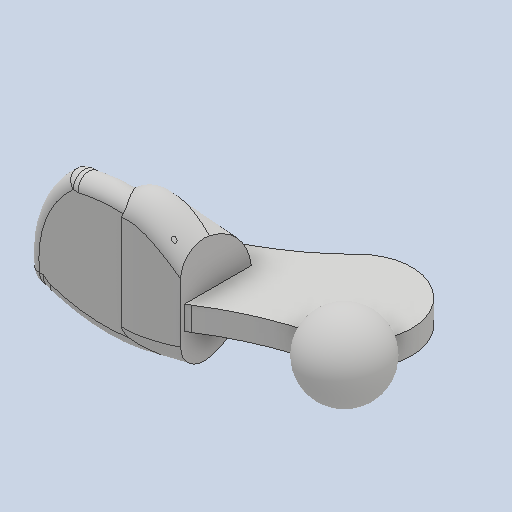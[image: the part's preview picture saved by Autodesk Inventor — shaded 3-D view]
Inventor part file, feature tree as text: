
AUTODESK INVENTOR PART (.ipt)
format: ipt  version: 2024.2 (Build 282272000, 272)  size: 452,096 bytes
history: native  units: mm
features: other x10, sketch x5, extrude x3, fillet x2, revolve x1, loft x1
ambient origin geometry x8: Origin, YZ Plane, XZ Plane, XY Plane, X Axis, Y Axis, Z Axis, Center Point
bodies: Body1 (feature_tree), Body2 (feature_tree), Body3 (feature_tree)
feature tree (22):
  other  "Твердое тело1"
  sketch  "Эскиз1"
  sketch  "Эскиз2"
  extrude  "Выдавливание1"  Depth=90.0mm
  revolve  "Вращение1"
  fillet  "Сопряжение1"  Radius=65.0mm
  extrude  "Выдавливание4"  Depth=40.0mm
  other  "РабПлоскость3"
  other  "РабПлоскость4"
  sketch  "Эскиз5"
  sketch  "Эскиз6"
  other  "РабПлоскость5"
  sketch  "Эскиз7"
  extrude  "Выдавливание6"  Depth=70.0mm
  other  "Разделение2"
  fillet  "Сопряжение4"  Radius=95.0mm
  loft  "Лофт5"
  other  "SRF1"
  other  "SRF2"
  other  "Ребра1"
  other  "ВыдавПврх1"
  other  "ВыдавПврх2"
